# Revit family: Kühlwanne Umluft GN1-1 - Zentral
name_source: partatom
category: Sonderausstattung
revit_build: Autodesk Revit 2015 (Build: 20140606_1530(x64)
units: mm (PartAtom-declared; Revit-internal decimal feet)

## types (4) — shared parameters
Artikelnr. = KWOU021100
Boden Stärke = 30 mm  [stored 0.0984252 ft]
Breite Technikgehäuse = 500 mm  [stored 1.64042 ft]
DN Flüssigkeitsleitung = 6 mm  [stored 0.019685 ft]
DN Saugleitung = 10 mm  [stored 0.0328084 ft]
DN Tauwasserabfluß = 25 mm  [stored 0.082021 ft]
Höhe = 485 mm  [stored 1.59121 ft]
Höhe Technikgehäuse = 100 mm  [stored 0.328084 ft]
Höhe Wanne = 385 mm  [stored 1.26312 ft]
Kapazität = 2 x GN 1/1, Tiefe 30 - 150 mm
Kälteleistung = 720 W / -10°C VT
Kältemittel = R404a
Material = Edelstahl AISI 304
Pole = 1
Rand Breite hinten = 59 mm
Rand Breite seitlich = 72 mm
Rand Breite vorne = 47 mm
Rand Stärke = 10 mm  [stored 0.0328084 ft]
Scheinleistung = 0 VA
Spannung = 230 V
Temp. Bereich = -1°C bis +5°C
Tiefe = 700 mm  [stored 2.29659 ft]
Tiefe ohne Rahmen = 668 mm  [stored 2.1916 ft]
Wand Seiten Stärke = 57 mm
Wand hinten Stärke = 85 mm
Wand vorne Stärke = 73 mm

## per-type parameters (varying)
| type | Breite | Breite ohne Rahmen | Watt |
| 2xGN1-1 | 800 mm  [stored 2.62467 ft] | 770 mm | 40 W |
| 3xGN1-1 | 1125 mm | 1095 mm | 40 W |
| 4xGN1-1 | 1455 mm  [stored 4.77362 ft] | 1425 mm  [stored 4.6752 ft] | 60 W |
| 5xGN1-1 | 1780 mm  [stored 5.8399 ft] | 1750 mm  [stored 5.74147 ft] | 80 W |

note: [stored X ft] marks values corroborated as IEEE doubles in the binary element streams (Revit-internal decimal feet)

## geometry (parser evidence)
native form markers: Blend x13, Sweep x3
no freeform markers — native parametric forms only
